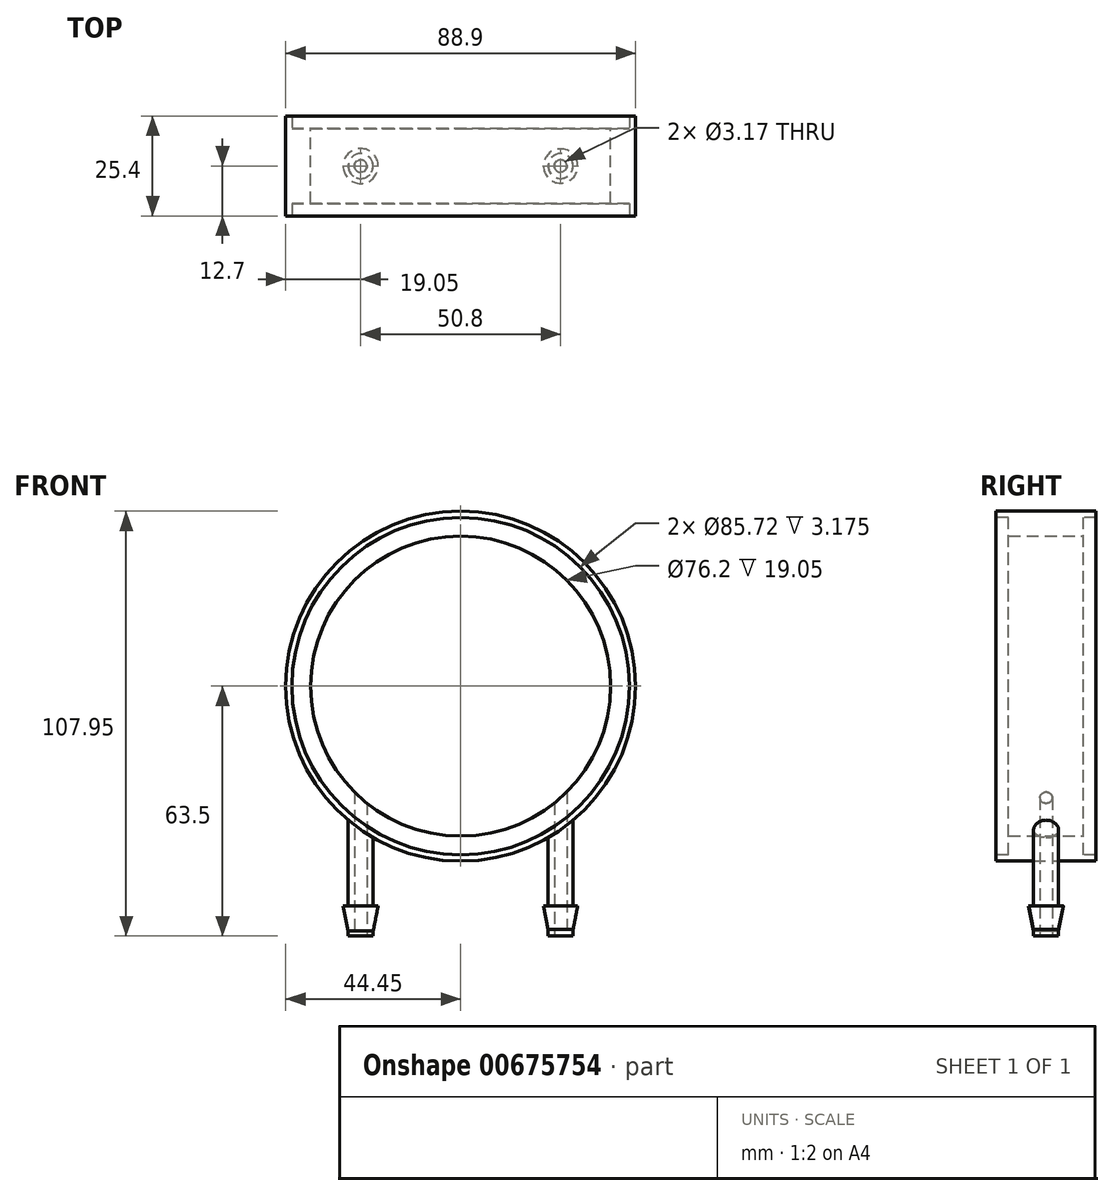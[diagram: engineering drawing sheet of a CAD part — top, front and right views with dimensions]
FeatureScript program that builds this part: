
annotation { "Feature Type Name" : "Feature", "Feature Type Description" : "" }
export const myFeature = defineFeature(function(context is Context, id is Id, definition is map)
    precondition{}
    {
        {
            var Q0;
            Q0=qCreatedBy(makeId("Front.planeOp"),FACE);
            var sketch = newSketch(context, id + "F0", { "sketchPlane" : qUnion([Q0])});
            skCircle(sketch, "E0", {"center": v(0, 0) * mm, "radius": 44.45 * mm});
            skSolve(sketch);
        }
        {
            var Q0;
            Q0=makeQuery(id+"F0.imprint","IMPRINT",FACE,{"disambiguationData":[TD([[makeQuery(id+"F0.imprint","IMPRINT",EDGE,{"derivedFrom":sQuery(id+"F0.wireOp",EDGE,"E0")}),1.0]])]});
            extrude(context, id + "F1", {"entities" : qUnion([Q0]), "endBound" : BoundingType.SYMMETRIC, "depth" : 25.4 * mm, "offsetDistance" : 25.4 * mm});
        }
        {
            var Q0;
            Q0=qCreatedBy(makeId("Front.planeOp"),FACE);
            var sketch = newSketch(context, id + "F2", { "sketchPlane" : qUnion([Q0])});
            skCircle(sketch, "E1", {"center": v(0, 0) * mm, "radius": 42.86 * mm});
            skSolve(sketch);
        }
        {
            var Q0;
            Q0=qCreatedBy(makeId("Front.planeOp"),FACE);
            var sketch = newSketch(context, id + "F3", { "sketchPlane" : qUnion([Q0])});
            skCircle(sketch, "E2", {"center": v(0, 0) * mm, "radius": 42.86 * mm});
            skSolve(sketch);
        }
        {
            var Q0;
            Q0 = qSketchRegion(id + "F2", true);
            extrude(context, id + "F4", {"entities" : qUnion([Q0]), "operationType" : NewBodyOperationType.REMOVE, "endBound" : BoundingType.SYMMETRIC, "oppositeDirection" : true, "depth" : 25.4 * mm, "offsetDistance" : 25.4 * mm});
        }
        {
            var Q0;
            Q0 = qSketchRegion(id + "F3", true);
            extrude(context, id + "F5", {"entities" : qUnion([Q0]), "operationType" : NewBodyOperationType.ADD, "endBound" : BoundingType.SYMMETRIC, "depth" : 19.05 * mm, "offsetDistance" : 25.4 * mm});
        }
        {
            var Q0;
            Q0=qCreatedBy(makeId("Front.planeOp"),FACE);
            var sketch = newSketch(context, id + "F6", { "sketchPlane" : qUnion([Q0])});
            skCircle(sketch, "E3", {"center": v(0, 0) * mm, "radius": 38.1 * mm});
            skSolve(sketch);
        }
        {
            var Q0;
            Q0=qCreatedBy(makeId("Top.planeOp"),FACE);
            var sketch = newSketch(context, id + "F7", { "sketchPlane" : qUnion([Q0])});
            skCircle(sketch, "E4", {"center": v(-25.4, 0) * mm, "radius": 3.18 * mm});
            skSolve(sketch);
        }
        {
            var Q0;
            Q0=qCreatedBy(makeId("Top.planeOp"),FACE);
            var sketch = newSketch(context, id + "F8", { "sketchPlane" : qUnion([Q0])});
            skCircle(sketch, "E5", {"center": v(25.4, 0) * mm, "radius": 3.18 * mm});
            skSolve(sketch);
        }
        {
            var Q0;
            Q0 = qSketchRegion(id + "F8", true);
            extrude(context, id + "F9", {"entities" : qUnion([Q0]), "operationType" : NewBodyOperationType.ADD, "oppositeDirection" : true, "depth" : 63.5 * mm, "offsetDistance" : 25.4 * mm});
        }
        {
            var Q0;
            Q0 = qSketchRegion(id + "F7", true);
            extrude(context, id + "F10", {"entities" : qUnion([Q0]), "operationType" : NewBodyOperationType.ADD, "oppositeDirection" : true, "depth" : 63.5 * mm, "offsetDistance" : 25.4 * mm});
        }
        {
            var Q0;
            Q0=qCreatedBy(makeId("Front.planeOp"),FACE);
            var sketch = newSketch(context, id + "F11", { "sketchPlane" : qUnion([Q0])});
            skLineSegment(sketch, "E6", {"start": v(28.48, -62.23) * mm, "end": v(29.75, -55.88) * mm});
            skLineSegment(sketch, "E7", {"start": v(29.75, -55.88) * mm, "end": v(28.48, -55.88) * mm});
            skLineSegment(sketch, "E8", {"start": v(28.48, -55.88) * mm, "end": v(28.48, -62.23) * mm});
            skSolve(sketch);
        }
        {
            var Q0;
            Q0=makeQuery(id+"F11.imprint","IMPRINT",FACE,{"disambiguationData":[TD([[makeQuery(id+"F11.imprint","IMPRINT",EDGE,{"derivedFrom":sQuery(id+"F11.wireOp",EDGE,"E6")}),1.0]])]});
            var Q1;
            Q1=makeQuery(id+"F9.opExtrude","CAP_EDGE",EDGE,{"disambiguationData":[OSD([sQuery(id+"F8.wireOp",EDGE,"E5")])],"isStart":false});
            revolve(context, id + "F12", {"operationType" : NewBodyOperationType.ADD, "entities" : qUnion([Q0]), "axis" : qUnion([Q1]), "revolveType" : RevolveType.FULL});
        }
        {
            var Q0;
            Q0=qCreatedBy(makeId("Front.planeOp"),FACE);
            var sketch = newSketch(context, id + "F13", { "sketchPlane" : qUnion([Q0])});
            skLineSegment(sketch, "E9", {"start": v(-22.23, -62.23) * mm, "end": v(-22.23, -55.88) * mm});
            skLineSegment(sketch, "E10", {"start": v(-22.23, -55.88) * mm, "end": v(-20.96, -55.88) * mm});
            skLineSegment(sketch, "E11", {"start": v(-22.23, -62.23) * mm, "end": v(-20.96, -55.88) * mm});
            skSolve(sketch);
        }
        {
            var Q0;
            Q0=makeQuery(id+"F13.imprint","IMPRINT",FACE,{"disambiguationData":[TD([[makeQuery(id+"F13.imprint","IMPRINT",EDGE,{"derivedFrom":sQuery(id+"F13.wireOp",EDGE,"E9")}),-1.0]])]});
            var Q1;
            Q1=makeQuery(id+"F10.opExtrude","CAP_EDGE",EDGE,{"disambiguationData":[OSD([sQuery(id+"F7.wireOp",EDGE,"E4")])],"isStart":false});
            revolve(context, id + "F14", {"operationType" : NewBodyOperationType.ADD, "entities" : qUnion([Q0]), "axis" : qUnion([Q1]), "revolveType" : RevolveType.FULL});
        }
        {
            var Q0;
            Q0=makeQuery(id+"F9.opExtrude","CAP_FACE",FACE,{"disambiguationData":[OSD([sQuery(id+"F8.wireOp",EDGE,"E5")])],"isStart":false});
            var sketch = newSketch(context, id + "F15", { "sketchPlane" : qUnion([Q0])});
            skCircle(sketch, "E12", {"center": v(25.4, 0) * mm, "radius": 1.59 * mm});
            skSolve(sketch);
        }
        {
            var Q0;
            Q0=makeQuery(id+"F15.imprint","IMPRINT",FACE,{"disambiguationData":[TD([[makeQuery(id+"F15.imprint","IMPRINT",EDGE,{"derivedFrom":sQuery(id+"F15.wireOp",EDGE,"E12")}),1.0]])]});
            extrude(context, id + "F16", {"entities" : qUnion([Q0]), "operationType" : NewBodyOperationType.REMOVE, "oppositeDirection" : true, "depth" : 76.2 * mm, "offsetDistance" : 25.4 * mm});
        }
        {
            var Q0;
            Q0=makeQuery(id+"F10.opExtrude","CAP_FACE",FACE,{"disambiguationData":[OSD([sQuery(id+"F7.wireOp",EDGE,"E4")])],"isStart":false});
            var sketch = newSketch(context, id + "F17", { "sketchPlane" : qUnion([Q0])});
            skCircle(sketch, "E13", {"center": v(-25.4, 0) * mm, "radius": 1.59 * mm});
            skSolve(sketch);
        }
        {
            var Q0;
            Q0=makeQuery(id+"F17.imprint","IMPRINT",FACE,{"disambiguationData":[TD([[makeQuery(id+"F17.imprint","IMPRINT",EDGE,{"derivedFrom":sQuery(id+"F17.wireOp",EDGE,"E13")}),1.0]])]});
            extrude(context, id + "F18", {"entities" : qUnion([Q0]), "operationType" : NewBodyOperationType.REMOVE, "oppositeDirection" : true, "depth" : 63.5 * mm, "offsetDistance" : 25.4 * mm});
        }
        {
            var Q0;
            Q0 = qSketchRegion(id + "F6", true);
            extrude(context, id + "F19", {"entities" : qUnion([Q0]), "operationType" : NewBodyOperationType.REMOVE, "endBound" : BoundingType.SYMMETRIC, "depth" : 25.4 * mm, "offsetDistance" : 25.4 * mm});
        }
    });
